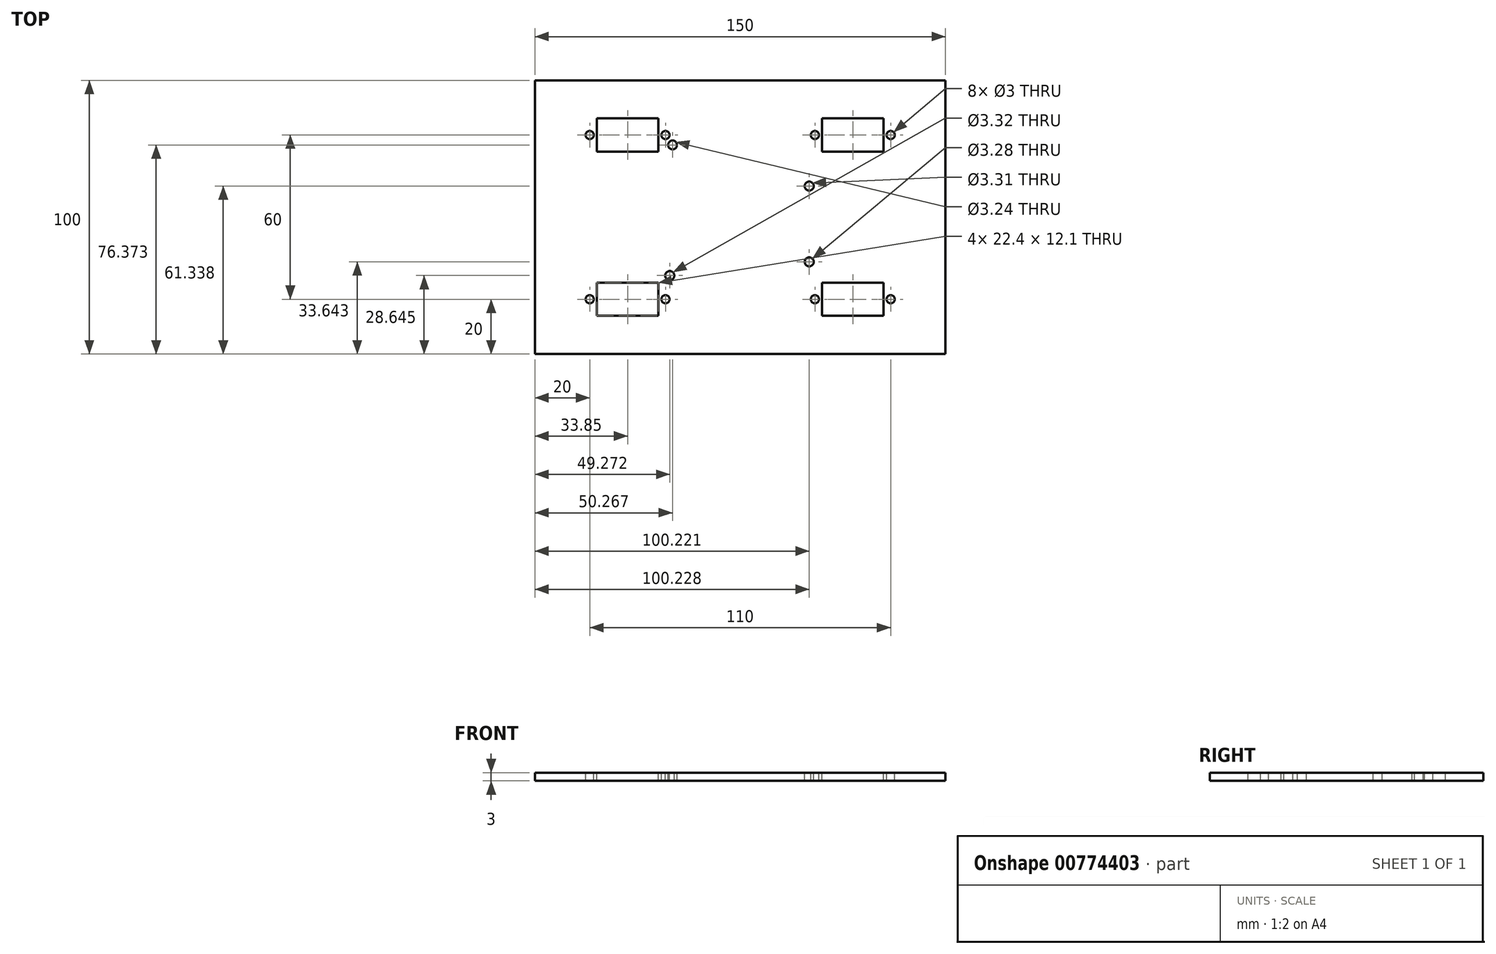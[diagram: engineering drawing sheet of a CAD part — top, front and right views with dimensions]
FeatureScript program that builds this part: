
annotation { "Feature Type Name" : "Feature", "Feature Type Description" : "" }
export const myFeature = defineFeature(function(context is Context, id is Id, definition is map)
    precondition{}
    {
        {
            var Q0;
            Q0=qCreatedBy(makeId("Top.planeOp"),FACE);
            var sketch = newSketch(context, id + "F0", { "sketchPlane" : qUnion([Q0])});
            skLineSegment(sketch, "E0.bottom", {"start": v(-75, 50) * mm, "end": v(75, 50) * mm});
            skLineSegment(sketch, "E0.top", {"start": v(-75, -50) * mm, "end": v(75, -50) * mm});
            skLineSegment(sketch, "E0.left", {"start": v(-75, 50) * mm, "end": v(-75, -50) * mm});
            skLineSegment(sketch, "E0.right", {"start": v(75, 50) * mm, "end": v(75, -50) * mm});
            skPoint(sketch, "E1", {"position": v(0, 0) * mm});
            skPoint(sketch, "E1.positionSnap0", {"position": v(-75, 0) * mm});
            skPoint(sketch, "E1.positionSnap1", {"position": v(0, 50) * mm});
            skSolve(sketch);
        }
        {
            var Q0;
            Q0 = qSketchRegion(id + "F0", true);
            extrude(context, id + "F1", {"entities" : qUnion([Q0]), "depth" : 3 * mm, "offsetDistance" : 25 * mm, "symmetric" : true});
        }
        {
            var Q0;
            Q0=makeQuery(id+"F1.opExtrude","CAP_FACE",FACE,{"disambiguationData":[OSD([sQuery(id+"F0.wireOp",EDGE,"E0.bottom"),sQuery(id+"F0.wireOp",EDGE,"E0.top"),sQuery(id+"F0.wireOp",EDGE,"E0.left"),sQuery(id+"F0.wireOp",EDGE,"E0.right")])],"isStart":false});
            var sketch = newSketch(context, id + "F2", { "sketchPlane" : qUnion([Q0])});
            skCircle(sketch, "E2", {"center": v(-55, -30) * mm, "radius": 1.5 * mm});
            skCircle(sketch, "E3", {"center": v(-27.3, -30) * mm, "radius": 1.5 * mm});
            skLineSegment(sketch, "E4.bottom", {"start": v(-52.35, -23.95) * mm, "end": v(-29.95, -23.95) * mm});
            skLineSegment(sketch, "E4.top", {"start": v(-52.35, -36.05) * mm, "end": v(-29.95, -36.05) * mm});
            skLineSegment(sketch, "E4.left", {"start": v(-52.35, -23.95) * mm, "end": v(-52.35, -36.05) * mm});
            skLineSegment(sketch, "E4.right", {"start": v(-29.95, -23.95) * mm, "end": v(-29.95, -36.05) * mm});
            skCircle(sketch, "E5", {"center": v(27.3, -30) * mm, "radius": 1.5 * mm});
            skCircle(sketch, "E6", {"center": v(55, -30) * mm, "radius": 1.5 * mm});
            skLineSegment(sketch, "E7.bottom", {"start": v(29.95, -23.95) * mm, "end": v(52.35, -23.95) * mm});
            skLineSegment(sketch, "E7.top", {"start": v(29.95, -36.05) * mm, "end": v(52.35, -36.05) * mm});
            skLineSegment(sketch, "E7.left", {"start": v(29.95, -23.95) * mm, "end": v(29.95, -36.05) * mm});
            skLineSegment(sketch, "E7.right", {"start": v(52.35, -23.95) * mm, "end": v(52.35, -36.05) * mm});
            skCircle(sketch, "E8", {"center": v(27.3, 30) * mm, "radius": 1.5 * mm});
            skCircle(sketch, "E9", {"center": v(55, 30) * mm, "radius": 1.5 * mm});
            skLineSegment(sketch, "E10.bottom", {"start": v(29.95, 36.05) * mm, "end": v(52.35, 36.05) * mm});
            skLineSegment(sketch, "E10.top", {"start": v(29.95, 23.95) * mm, "end": v(52.35, 23.95) * mm});
            skLineSegment(sketch, "E10.left", {"start": v(29.95, 36.05) * mm, "end": v(29.95, 23.95) * mm});
            skLineSegment(sketch, "E10.right", {"start": v(52.35, 36.05) * mm, "end": v(52.35, 23.95) * mm});
            skCircle(sketch, "E11", {"center": v(-55, 30) * mm, "radius": 1.5 * mm});
            skCircle(sketch, "E12", {"center": v(-27.3, 30) * mm, "radius": 1.5 * mm});
            skLineSegment(sketch, "E13.bottom", {"start": v(-52.35, 36.05) * mm, "end": v(-29.95, 36.05) * mm});
            skLineSegment(sketch, "E13.top", {"start": v(-52.35, 23.95) * mm, "end": v(-29.95, 23.95) * mm});
            skLineSegment(sketch, "E13.left", {"start": v(-52.35, 36.05) * mm, "end": v(-52.35, 23.95) * mm});
            skLineSegment(sketch, "E13.right", {"start": v(-29.95, 36.05) * mm, "end": v(-29.95, 23.95) * mm});
            skSolve(sketch);
        }
        {
            var Q0;
            Q0 = qSketchRegion(id + "F2", true);
            extrude(context, id + "F3", {"entities" : qUnion([Q0]), "operationType" : NewBodyOperationType.REMOVE, "endBound" : BoundingType.THROUGH_ALL, "oppositeDirection" : true, "depth" : 25 * mm, "offsetDistance" : 25 * mm});
        }
        {
            var Q0;
            Q0=makeQuery(id+"F1.opExtrude","CAP_FACE",FACE,{"disambiguationData":[OSD([sQuery(id+"F0.wireOp",EDGE,"E0.bottom"),sQuery(id+"F0.wireOp",EDGE,"E0.top"),sQuery(id+"F0.wireOp",EDGE,"E0.left"),sQuery(id+"F0.wireOp",EDGE,"E0.right")])],"isStart":false});
            var sketch = newSketch(context, id + "F4", { "sketchPlane" : qUnion([Q0])});
            skLineSegment(sketch, "E14", {"start": v(-24.73, 28) * mm, "end": v(-24.73, 24.7) * mm, "construction": true});
            skLineSegment(sketch, "E15", {"start": v(-26.38, 26.37) * mm, "end": v(-23.09, 26.37) * mm, "construction": true});
            skCircle(sketch, "E16", {"center": v(-24.73, 26.37) * mm, "radius": 1.62 * mm});
            skLineSegment(sketch, "E17", {"start": v(23.59, 11.35) * mm, "end": v(26.88, 11.35) * mm, "construction": true});
            skLineSegment(sketch, "E18", {"start": v(25.22, 13) * mm, "end": v(25.22, 9.69) * mm, "construction": true});
            skCircle(sketch, "E19", {"center": v(25.22, 11.34) * mm, "radius": 1.66 * mm});
            skLineSegment(sketch, "E20", {"start": v(25.23, -14.7) * mm, "end": v(25.23, -18) * mm, "construction": true});
            skLineSegment(sketch, "E21", {"start": v(23.59, -16.36) * mm, "end": v(26.88, -16.36) * mm, "construction": true});
            skCircle(sketch, "E22", {"center": v(25.23, -16.36) * mm, "radius": 1.64 * mm});
            skLineSegment(sketch, "E23", {"start": v(-25.73, -19.7) * mm, "end": v(-25.73, -23) * mm, "construction": true});
            skLineSegment(sketch, "E24", {"start": v(-27.36, -21.35) * mm, "end": v(-24.07, -21.35) * mm, "construction": true});
            skCircle(sketch, "E25", {"center": v(-25.73, -21.35) * mm, "radius": 1.66 * mm});
            skSolve(sketch);
        }
        {
            var Q0;
            Q0 = qSketchRegion(id + "F4", true);
            var Q1;
            Q1=sQuery(id+"F4.wireOp",EDGE,"E16");
            var Q2;
            Q2=sQuery(id+"F4.wireOp",EDGE,"E19");
            var Q3;
            Q3=sQuery(id+"F4.wireOp",EDGE,"E22");
            var Q4;
            Q4=sQuery(id+"F4.wireOp",EDGE,"E25");
            extrude(context, id + "F5", {"entities" : qUnion([Q0]), "operationType" : NewBodyOperationType.REMOVE, "surfaceEntities" : qUnion([Q1, Q2, Q3, Q4]), "endBound" : BoundingType.THROUGH_ALL, "oppositeDirection" : true, "depth" : 25 * mm, "offsetDistance" : 25 * mm});
        }
    });
